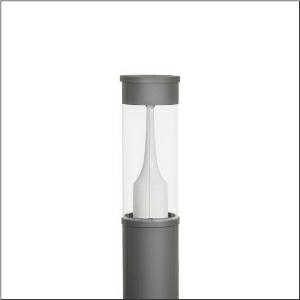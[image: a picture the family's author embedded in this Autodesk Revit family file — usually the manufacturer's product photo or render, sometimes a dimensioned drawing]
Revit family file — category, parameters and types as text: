
# Revit family: city-light_120_iq___pl1_2s_5xa5285jf14h_c322
name_source: partatom
category: Lighting Fixtures
units: mm (PartAtom-declared; Revit-internal decimal feet)

## family parameters
Cut with Voids When Loaded = No
Host = Face
Light Source = No
Part Type = Normal
Room Calculation Point = No
Round Connector Dimension = Use Diameter
Shared = No

## types (1)
- --- (1 x LED, 2970 lm, 19.3 W, 3000K)
    Apparent Load = 19 VA
    CIE Flux Codes = 23 62 94 96 100
    Color Rendering = 70
    Color Temperature = 3000K
    Default Elevation = 1800 mm
    Description = City-Light 120 iQ, bollard luminaire, Module 540 iQ-SR, primary light control with 3 zone facetted reflector, of plastic, silver coated, highly specular, structured, primary optical cover: cover, of PMMA, transparent, light distribution: PL1.2s, primary light characteristic: symmetric, LED, High Power LED, rated luminous flux: 2.970lm, luminous efficacy: 154lm/W, light colour: 730, colour temperature: 3000K, control gear: iQ Street-Remote, control: Auto-Match, Temp-Guard, Lumen-Switch, Night-Set, Smart-Wire, Light-Fading, Desk-Remote (wireless, voltage-free reading and setting of iQ features in the workshop via application-optimized NFC function/RFID function), optimised constant luminous flux control (CLO 2.0), Street-Remote, pre-setting: logarithmic dimming characteristic, with terminal, 6-pole, max. 2.5mm², mains connection: 230..240V, AC, 50/60Hz, start of lifetime: 19W, end of service life: 21W, reduction: 10W, luminaire housing, cylindrical, of extruded aluminium section, coated, Siteco® metallic grey (DB 702S), length: 1.200mm, diameter: 200mm, Module 540 iQ-SR, traffic white (RAL 9016), equipment: standard, protection rating (complete): IP54, insulation class (complete): insulation class II (safety insulation), certification: CE, ENEC, VDE, packaging unit: 1 piece

Light Distribution: PL1.2s
    Height = 500 mm
    Lamp = 1 x LED
    Lamp Light Flux = 2970 lm
    Lamp Power = 19.3 W
    Lamp count = 1
    Length = 200 mm  [stored 0.656168 ft]
    Luminous efficacy = 154 lm/W
    Manufacturer = Siteco
    ModVariant = No
    Model = 5XA5285JF14H
    Mounting Place = Floor
    Mounting Type = Freestanding
    Number of Poles = 1
    OnlyDefault = Yes
    Power Factor = 1
    Product Name = City-Light 120 iQ | PL1.2s
    Product group = bollard luminaire
    ProductGroupID = 1304
    Protection Class = Protection class II
    Protection Degree = IP 54
    RLX_Detail_Level = 1
    RLX_Emergency_Light_Flux = 0 lm
    RLX_Emergency_Type = 0
    RLX_Emergency_Type_DB = No
    RlxData = <blob elided: 22321 chars, md5=5de6af85>
    Socket = socket
    Standby Power = 0 W
    System Light Flux = 2970 lm
    System Power = 19 W
    Type Comments = factory setting: luminous flux: 100 % | dim-lin: 254 | 403 mA
    Type Image = l_1006922.jpg
    URL = http://relux.com
    VarID = @adj_166673
    Voltage = 0 V
    Weight = 0.00 kg
    Width = 0 mm  [stored 0 ft]

note: [stored X ft] marks values corroborated as IEEE doubles in the binary element streams (Revit-internal decimal feet)

## geometry (parser evidence)
native form markers: Blend x4, Sweep x9
no freeform markers — native parametric forms only
